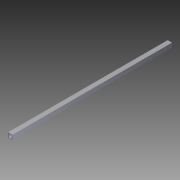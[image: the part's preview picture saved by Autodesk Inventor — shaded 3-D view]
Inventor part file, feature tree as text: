
AUTODESK INVENTOR PART (.ipt)
format: ipt  version: 2012 (Build 160160000, 160)  size: 74,240 bytes
history: native  units: in
note: dims shown in document units (in); Inventor stores cm internally (conversion verified against a paired STEP export)
features: extrude x1, sketch x1
ambient origin geometry x8: Origin, YZ Plane, XZ Plane, XY Plane, X Axis, Y Axis, Z Axis, Center Point
bodies: Solid1 (feature_tree)
feature tree (2):
  extrude  "Extrusion1"  Depth=1.0in
  sketch  "Sketch1"  dims[d0=1.0in d1=1.0in d2=0.125in d3=0.125in d4=0.125in d5=0.125in d6=36.75in d7=0.0in]
